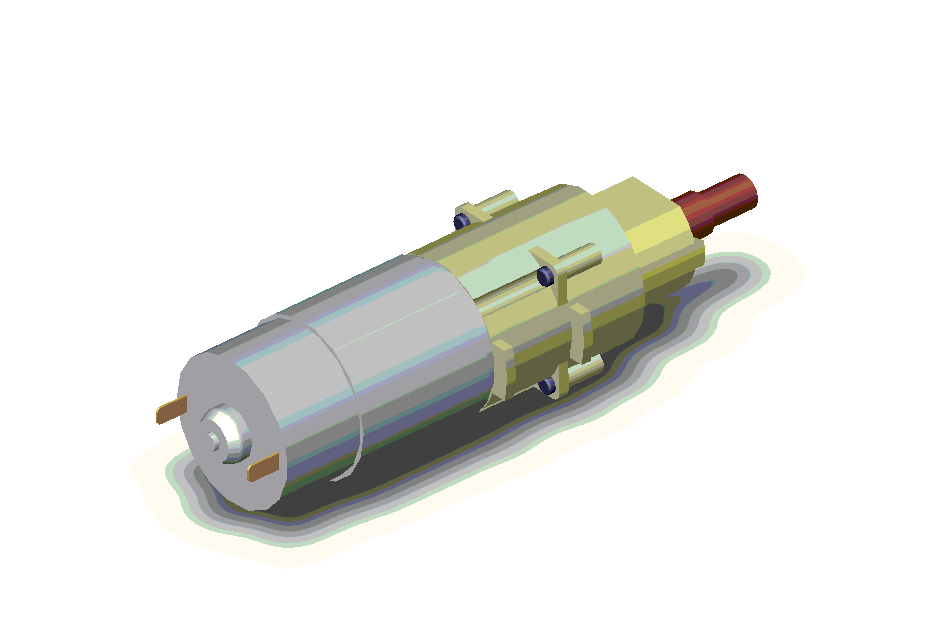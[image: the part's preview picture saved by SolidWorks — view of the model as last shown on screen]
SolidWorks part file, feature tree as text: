
SOLIDWORKS PART (.sldprt)
format: sldprt  version: not decoded by parser v0  size: 745,984 bytes
history: native  units: mm
features: sketch x20, extrude x17, cut_extrude x3, fillet x3, plane x2, chamfer x1 + 1 further entry (+7 scaffold rows collapsed)
feature tree (54):
  "Annotations"  RD1=36.084585mm
  scaffold x7  (default folders/planes/origin — collapsed)
  sketch  "Sketch1"  dims[D1=9.525mm]
  extrude  "Base-Extrude"  Depth=13.7922mm
  sketch  "Sketch2"  dims[D1=12.065mm]
  extrude  "Boss-Extrude1"  Depth=6.35mm
  sketch  "Sketch3"  dims[c1.D5=15.748mm c1.D2=15.494mm c1.D3=15.494mm c1.D1=29.718mm c2.D2=24.384mm c2.D3=24.384mm c2.D4=17.78mm c2.D1=~17.98066mm c3.D2=24.384mm]
  extrude  "Boss-Extrude2"  Depth=21.844mm
  sketch  "Sketch5"  dims[D1=42.8498mm D2=~48.525307mm D3=41.275mm]
  extrude  "Boss-Extrude3"  Depth=48.26mm
  sketch  "Sketch19"  dims[D1=17.78mm D2=~29.853247mm D3=3.556mm D4=7.112mm]
  extrude  "Boss-Extrude11"  Depth=2.9464mm
  sketch  "Sketch20"  dims[D3=2.54mm D4=2.54mm D1=11.811mm D2=11.811mm]
  cut_extrude  "Cut-Extrude1"  Depth=21.59mm
  sketch  "Sketch21"  dims[D1=12.065mm]
  extrude  "Boss-Extrude12"  Depth=13.462mm
  sketch  "Sketch22"
  extrude  "Boss-Extrude13"  Depth=28.575mm
  sketch  "Sketch23"  dims[D1=4.572mm]
  cut_extrude  "Cut-Extrude2"  Depth=21.59mm
  plane  "Plane1"  Offset=23.495mm
  sketch  "Sketch25"  dims[D5=2.54mm D1=19.685mm D2=39.37mm D3=39.37mm D4=19.685mm]
  extrude  "Boss-Extrude14"  Depth=3.048mm
  sketch  "Sketch26"  dims[D1=5.842mm D2=5.842mm D3=5.842mm D4=5.842mm D5=3.81mm D6=3.81mm D7=3.81mm D8=3.81mm D9=3.81mm D10=3.81mm D11=3.81mm D12=3.81mm]
  extrude  "Boss-Extrude15"  Depth=12.192mm
  sketch  "Sketch28"  dims[D1=51.816mm D2=7.366mm D3=14.732mm]
  extrude  "Boss-Extrude16"  Depth=2.921mm
  sketch  "Sketch29"
  extrude  "Boss-Extrude17"  Depth=2.794mm
  sketch  "Sketch30"  dims[D1=42.164mm]
  extrude  "Boss-Extrude18"  Depth=66.802mm
  plane  "Plane2"  Offset=2.54mm
  sketch  "Sketch31"  dims[D1=44.45mm D2=7.62mm D3=3.81mm D4=~11.852332mm]
  extrude  "Boss-Extrude19"  Depth=40.64mm
  sketch  "Sketch32"  dims[D1=15.24mm]
  extrude  "Boss-Extrude20"  Depth=6.096mm
  chamfer  "Chamfer1"  Distance=3.048mm Angle=30deg
  fillet  "Fillet1"  Radius=2.54mm
  sketch  "Sketch33"  dims[D1=4.953mm]
  extrude  "Boss-Extrude21"  Depth=1.524mm
  sketch  "Sketch34"  dims[D1=5.588mm D2=5.588mm D3=5.588mm D4=5.588mm]
  cut_extrude  "Cut-Extrude3"  [1 undecoded]
  sketch  "Sketch35"  dims[D1=5.08mm D2=5.08mm D3=5.08mm D4=5.08mm]
  extrude  "Boss-Extrude22"  Depth=1.905mm
  fillet  "Fillet2"  Radius=0.762mm
  sketch  "Sketch36"  dims[D1=35.56mm D2=17.78mm D3=4.826mm D4=4.826mm D5=2.413mm D6=2.54mm D7=0.635mm D8=0.635mm]
  extrude  "Boss-Extrude23"  Depth=9.652mm
  fillet  "Fillet3"  Radius=1.27mm
decode coverage: 41 of 44 modeling features carry decoded parameters; 1 rows unclassified (native names shown)
note: ~ marks probable driven/reference dimensions
note: 1 parameter value undecoded
note: suppression state not decoded; provenance and decode notes live in map.json
